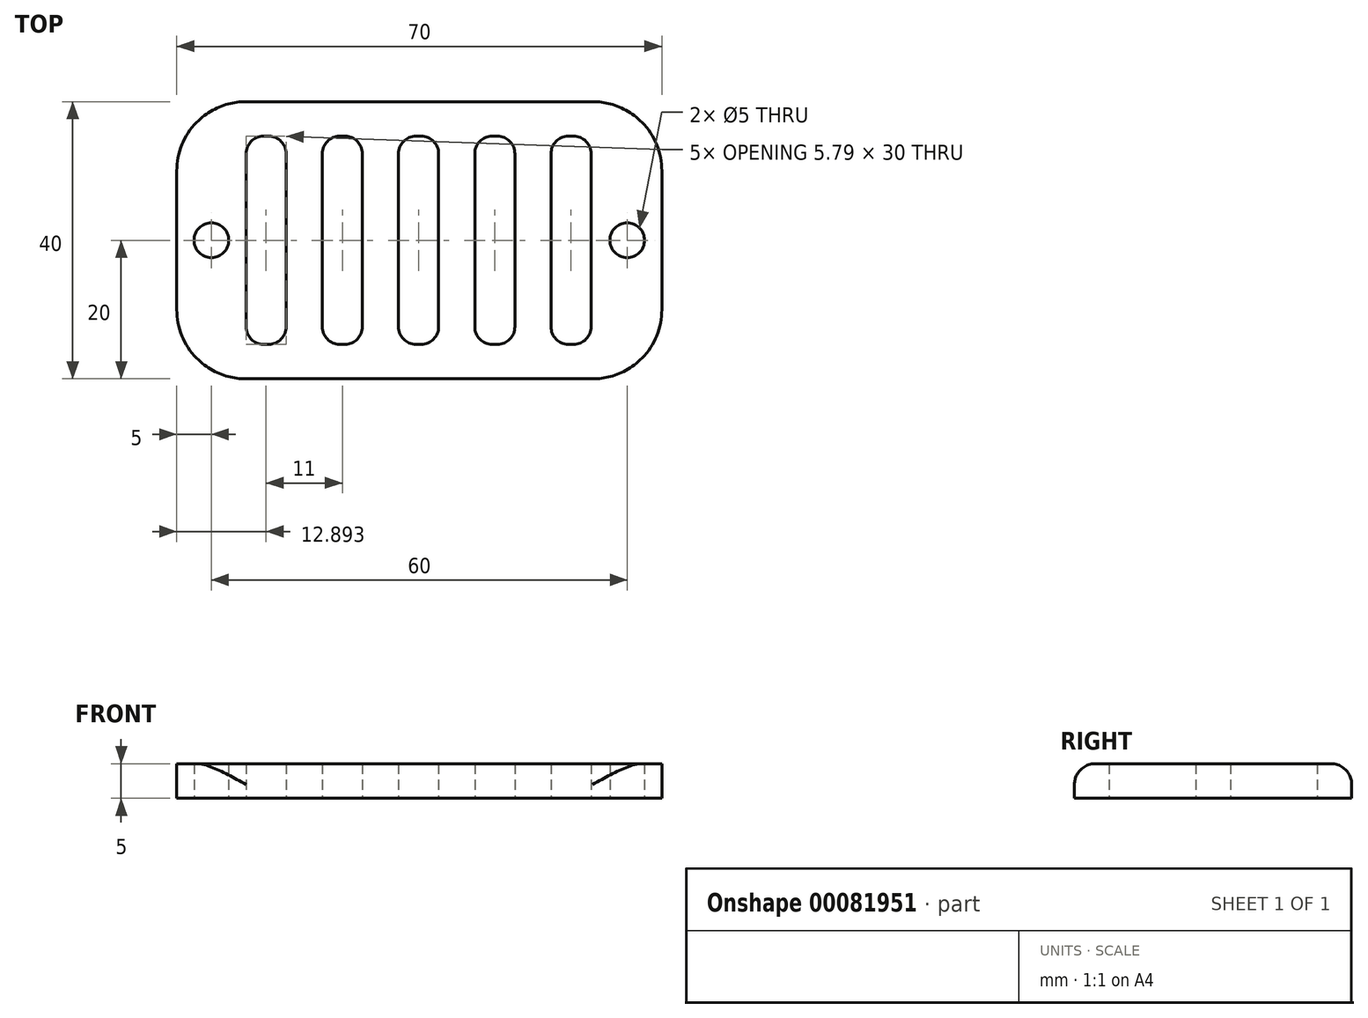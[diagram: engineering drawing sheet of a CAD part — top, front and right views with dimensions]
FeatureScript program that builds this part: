
annotation { "Feature Type Name" : "Feature", "Feature Type Description" : "" }
export const myFeature = defineFeature(function(context is Context, id is Id, definition is map)
    precondition{}
    {
        {
            var Q0;
            Q0=qCreatedBy(makeId("Top.planeOp"),FACE);
            var sketch = newSketch(context, id + "F0", { "sketchPlane" : qUnion([Q0])});
            skLineSegment(sketch, "E0.rect.bottom", {"start": v(-35, 20) * mm, "end": v(35, 20) * mm});
            skLineSegment(sketch, "E0.rect.top", {"start": v(-35, -20) * mm, "end": v(35, -20) * mm});
            skLineSegment(sketch, "E0.rect.left", {"start": v(-35, 20) * mm, "end": v(-35, -20) * mm});
            skLineSegment(sketch, "E0.rect.right", {"start": v(35, 20) * mm, "end": v(35, -20) * mm});
            skPoint(sketch, "E0.rect.middle", {"position": v(0, 0) * mm});
            skCircle(sketch, "E1", {"center": v(-30, 0) * mm, "radius": 2.5 * mm});
            skCircle(sketch, "E2", {"center": v(30, 0) * mm, "radius": 2.5 * mm});
            skLineSegment(sketch, "E3.rect.bottom", {"start": v(-22.5, 15) * mm, "end": v(-21.71, 15) * mm});
            skLineSegment(sketch, "E3.rect.top", {"start": v(-22.5, -15) * mm, "end": v(-21.71, -15) * mm});
            skLineSegment(sketch, "E3.rect.left", {"start": v(-25, 12.5) * mm, "end": v(-25, -12.5) * mm});
            skLineSegment(sketch, "E3.rect.right", {"start": v(-19.21, 12.5) * mm, "end": v(-19.21, -12.5) * mm});
            skPoint(sketch, "E3.rect.middle", {"position": v(-22.1, 0) * mm});
            skPoint(sketch, "E4.visualSharp", {"position": v(-19.21, 15) * mm});
            skArc(sketch, "E4.filletArc", {"start": v(-19.21, 12.5) * mm, "mid": v(-19.95, 14.27) * mm, "end": v(-21.71, 15) * mm});
            skPoint(sketch, "E5.visualSharp", {"position": v(-25, 15) * mm});
            skArc(sketch, "E5.filletArc", {"start": v(-22.5, 15) * mm, "mid": v(-24.27, 14.27) * mm, "end": v(-25, 12.5) * mm});
            skPoint(sketch, "E6.visualSharp", {"position": v(-25, -15) * mm});
            skArc(sketch, "E6.filletArc", {"start": v(-25, -12.5) * mm, "mid": v(-24.27, -14.27) * mm, "end": v(-22.5, -15) * mm});
            skPoint(sketch, "E7.visualSharp", {"position": v(-19.21, -15) * mm});
            skArc(sketch, "E7.filletArc", {"start": v(-21.71, -15) * mm, "mid": v(-19.95, -14.27) * mm, "end": v(-19.21, -12.5) * mm});
            skPoint(sketch, "E8.1.0.0", {"position": v(-14, -15) * mm});
            skPoint(sketch, "E8.1.0.1", {"position": v(-8.21, -15) * mm});
            skLineSegment(sketch, "E8.1.0.2", {"start": v(-14, 12.5) * mm, "end": v(-14, -12.5) * mm});
            skLineSegment(sketch, "E8.1.0.3", {"start": v(-8.21, 12.5) * mm, "end": v(-8.21, -12.5) * mm});
            skPoint(sketch, "E8.1.0.4", {"position": v(-11.1, 0) * mm});
            skPoint(sketch, "E8.1.0.5", {"position": v(-8.21, 15) * mm});
            skPoint(sketch, "E8.1.0.6", {"position": v(-14, 15) * mm});
            skArc(sketch, "E8.1.0.7", {"start": v(-11.5, 15) * mm, "mid": v(-13.27, 14.27) * mm, "end": v(-14, 12.5) * mm});
            skArc(sketch, "E8.1.0.8", {"start": v(-8.21, 12.5) * mm, "mid": v(-8.95, 14.27) * mm, "end": v(-10.71, 15) * mm});
            skArc(sketch, "E8.1.0.9", {"start": v(-14, -12.5) * mm, "mid": v(-13.27, -14.27) * mm, "end": v(-11.5, -15) * mm});
            skArc(sketch, "E8.1.0.10", {"start": v(-10.71, -15) * mm, "mid": v(-8.95, -14.27) * mm, "end": v(-8.21, -12.5) * mm});
            skLineSegment(sketch, "E8.1.0.11", {"start": v(-11.5, 15) * mm, "end": v(-10.71, 15) * mm});
            skLineSegment(sketch, "E8.1.0.12", {"start": v(-11.5, -15) * mm, "end": v(-10.71, -15) * mm});
            skPoint(sketch, "E8.2.0.0", {"position": v(-3, -15) * mm});
            skPoint(sketch, "E8.2.0.1", {"position": v(2.79, -15) * mm});
            skLineSegment(sketch, "E8.2.0.2", {"start": v(-3, 12.5) * mm, "end": v(-3, -12.5) * mm});
            skLineSegment(sketch, "E8.2.0.3", {"start": v(2.79, 12.5) * mm, "end": v(2.79, -12.5) * mm});
            skPoint(sketch, "E8.2.0.4", {"position": v(-0.1, 0) * mm});
            skPoint(sketch, "E8.2.0.5", {"position": v(2.79, 15) * mm});
            skPoint(sketch, "E8.2.0.6", {"position": v(-3, 15) * mm});
            skArc(sketch, "E8.2.0.7", {"start": v(-0.5, 15) * mm, "mid": v(-2.27, 14.27) * mm, "end": v(-3, 12.5) * mm});
            skArc(sketch, "E8.2.0.8", {"start": v(2.79, 12.5) * mm, "mid": v(2.05, 14.27) * mm, "end": v(0.29, 15) * mm});
            skArc(sketch, "E8.2.0.9", {"start": v(-3, -12.5) * mm, "mid": v(-2.27, -14.27) * mm, "end": v(-0.5, -15) * mm});
            skArc(sketch, "E8.2.0.10", {"start": v(0.29, -15) * mm, "mid": v(2.05, -14.27) * mm, "end": v(2.79, -12.5) * mm});
            skLineSegment(sketch, "E8.2.0.11", {"start": v(-0.5, 15) * mm, "end": v(0.29, 15) * mm});
            skLineSegment(sketch, "E8.2.0.12", {"start": v(-0.5, -15) * mm, "end": v(0.29, -15) * mm});
            skPoint(sketch, "E8.3.0.0", {"position": v(8, -15) * mm});
            skPoint(sketch, "E8.3.0.1", {"position": v(13.79, -15) * mm});
            skLineSegment(sketch, "E8.3.0.2", {"start": v(8, 12.5) * mm, "end": v(8, -12.5) * mm});
            skLineSegment(sketch, "E8.3.0.3", {"start": v(13.79, 12.5) * mm, "end": v(13.79, -12.5) * mm});
            skPoint(sketch, "E8.3.0.4", {"position": v(10.9, 0) * mm});
            skPoint(sketch, "E8.3.0.5", {"position": v(13.79, 15) * mm});
            skPoint(sketch, "E8.3.0.6", {"position": v(8, 15) * mm});
            skArc(sketch, "E8.3.0.7", {"start": v(10.5, 15) * mm, "mid": v(8.73, 14.27) * mm, "end": v(8, 12.5) * mm});
            skArc(sketch, "E8.3.0.8", {"start": v(13.79, 12.5) * mm, "mid": v(13.05, 14.27) * mm, "end": v(11.29, 15) * mm});
            skArc(sketch, "E8.3.0.9", {"start": v(8, -12.5) * mm, "mid": v(8.73, -14.27) * mm, "end": v(10.5, -15) * mm});
            skArc(sketch, "E8.3.0.10", {"start": v(11.29, -15) * mm, "mid": v(13.05, -14.27) * mm, "end": v(13.79, -12.5) * mm});
            skLineSegment(sketch, "E8.3.0.11", {"start": v(10.5, 15) * mm, "end": v(11.29, 15) * mm});
            skLineSegment(sketch, "E8.3.0.12", {"start": v(10.5, -15) * mm, "end": v(11.29, -15) * mm});
            skPoint(sketch, "E8.4.0.0", {"position": v(19, -15) * mm});
            skPoint(sketch, "E8.4.0.1", {"position": v(24.79, -15) * mm});
            skLineSegment(sketch, "E8.4.0.2", {"start": v(19, 12.5) * mm, "end": v(19, -12.5) * mm});
            skLineSegment(sketch, "E8.4.0.3", {"start": v(24.79, 12.5) * mm, "end": v(24.79, -12.5) * mm});
            skPoint(sketch, "E8.4.0.4", {"position": v(21.9, 0) * mm});
            skPoint(sketch, "E8.4.0.5", {"position": v(24.79, 15) * mm});
            skPoint(sketch, "E8.4.0.6", {"position": v(19, 15) * mm});
            skArc(sketch, "E8.4.0.7", {"start": v(21.5, 15) * mm, "mid": v(19.73, 14.27) * mm, "end": v(19, 12.5) * mm});
            skArc(sketch, "E8.4.0.8", {"start": v(24.79, 12.5) * mm, "mid": v(24.05, 14.27) * mm, "end": v(22.29, 15) * mm});
            skArc(sketch, "E8.4.0.9", {"start": v(19, -12.5) * mm, "mid": v(19.73, -14.27) * mm, "end": v(21.5, -15) * mm});
            skArc(sketch, "E8.4.0.10", {"start": v(22.29, -15) * mm, "mid": v(24.05, -14.27) * mm, "end": v(24.79, -12.5) * mm});
            skLineSegment(sketch, "E8.4.0.11", {"start": v(21.5, 15) * mm, "end": v(22.29, 15) * mm});
            skLineSegment(sketch, "E8.4.0.12", {"start": v(21.5, -15) * mm, "end": v(22.29, -15) * mm});
            skLineSegment(sketch, "E8.direction1", {"start": v(-25, -15) * mm, "end": v(-14, -15) * mm, "construction": true});
            skSolve(sketch);
        }
        {
            var Q0;
            Q0=qSketchRegion(id+"F0",true);
            extrude(context, id + "F1", {"entities" : qUnion([Q0]), "depth" : 5 * mm});
        }
        {
            var Q0;
            Q0=makeQuery(id+"F1.opExtrude","SWEPT_EDGE",EDGE,{"disambiguationData":[OSD([sQuery(id+"F0.wireOp",EDGE,"E0.rect.bottom"),sQuery(id+"F0.wireOp",EDGE,"E0.rect.left")])]});
            var Q1;
            Q1=makeQuery(id+"F1.opExtrude","SWEPT_EDGE",EDGE,{"disambiguationData":[OSD([sQuery(id+"F0.wireOp",EDGE,"E0.rect.top"),sQuery(id+"F0.wireOp",EDGE,"E0.rect.left")])]});
            var Q2;
            Q2=makeQuery(id+"F1.opExtrude","SWEPT_EDGE",EDGE,{"disambiguationData":[OSD([sQuery(id+"F0.wireOp",EDGE,"E0.rect.top"),sQuery(id+"F0.wireOp",EDGE,"E0.rect.right")])]});
            var Q3;
            Q3=makeQuery(id+"F1.opExtrude","SWEPT_EDGE",EDGE,{"disambiguationData":[OSD([sQuery(id+"F0.wireOp",EDGE,"E0.rect.bottom"),sQuery(id+"F0.wireOp",EDGE,"E0.rect.right")])]});
            fillet(context, id + "F2", {"entities" : qUnion([Q0, Q1, Q2, Q3]), "radius" : 10 * mm, "tangentPropagation" : true, "allowEdgeOverflow" : false});
        }
        {
            var Q0;
            Q0=makeQuery(id+"F1.opExtrude","CAP_EDGE",EDGE,{"disambiguationData":[OSD([sQuery(id+"F0.wireOp",EDGE,"E0.rect.top")])],"isStart":false});
            var Q1;
            Q1=makeQuery(id+"F1.opExtrude","CAP_EDGE",EDGE,{"disambiguationData":[OSD([sQuery(id+"F0.wireOp",EDGE,"E0.rect.bottom")])],"isStart":false});
            fillet(context, id + "F3", {"entities" : qUnion([Q0, Q1]), "radius" : 3 * mm, "allowEdgeOverflow" : false});
        }
    });
